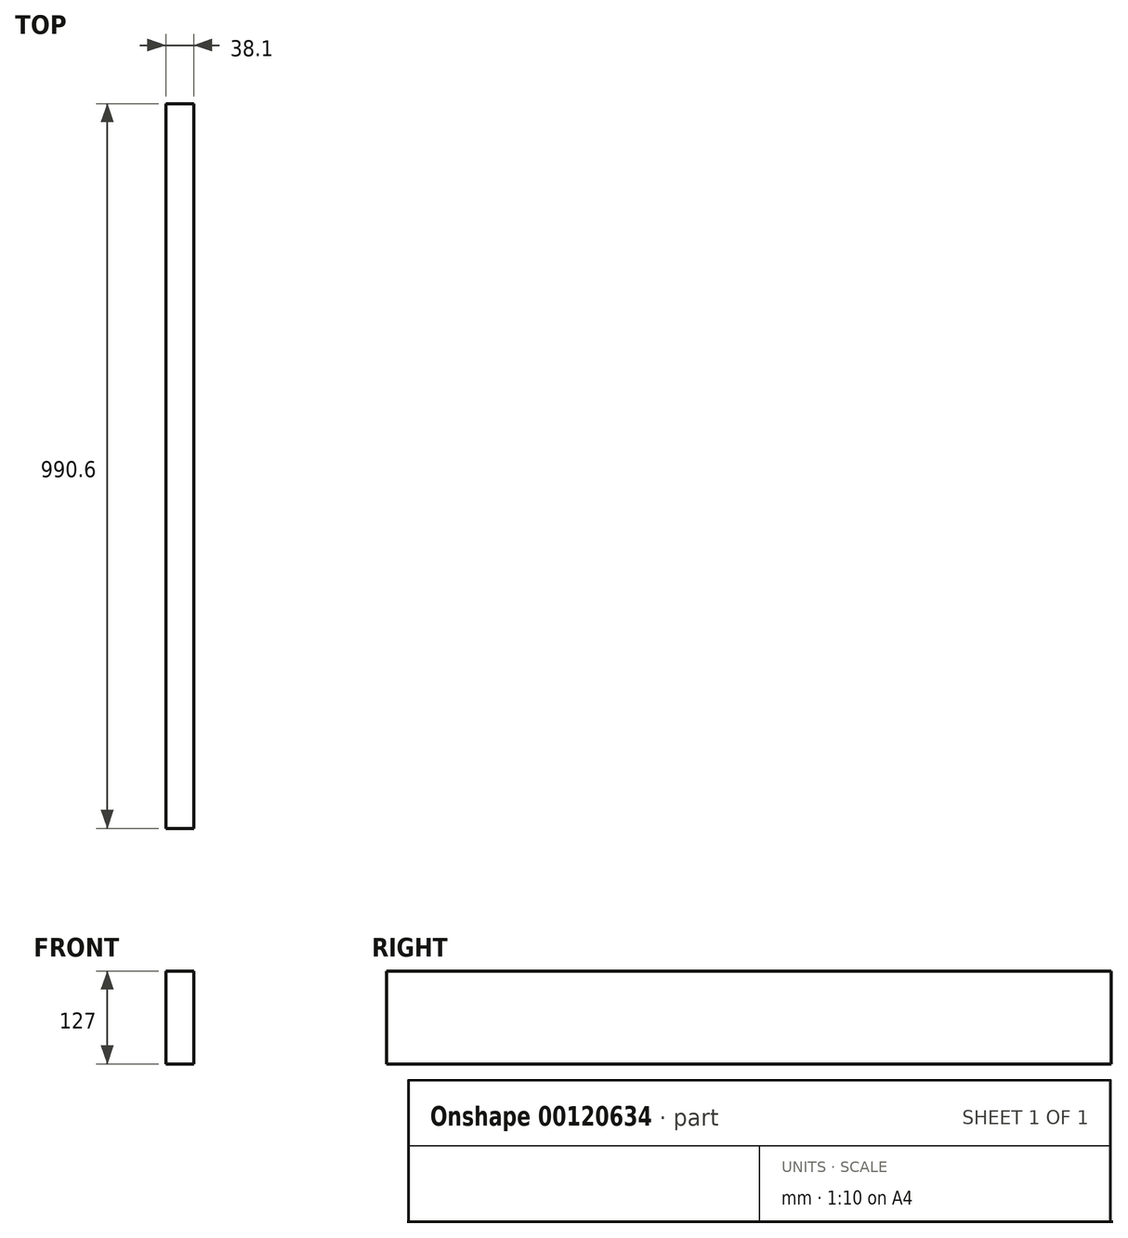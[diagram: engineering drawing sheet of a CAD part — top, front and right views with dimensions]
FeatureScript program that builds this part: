
annotation { "Feature Type Name" : "Feature", "Feature Type Description" : "" }
export const myFeature = defineFeature(function(context is Context, id is Id, definition is map)
    precondition{}
    {
        {
            var Q0;
            Q0=qCreatedBy(makeId("Top.planeOp"),FACE);
            var sketch = newSketch(context, id + "F0", { "sketchPlane" : qUnion([Q0])});
            skLineSegment(sketch, "E0.bottom", {"start": v(-19.05, -495.3) * mm, "end": v(19.05, -495.3) * mm});
            skLineSegment(sketch, "E0.top", {"start": v(-19.05, 495.3) * mm, "end": v(19.05, 495.3) * mm});
            skLineSegment(sketch, "E0.left", {"start": v(-19.05, -495.3) * mm, "end": v(-19.05, 495.3) * mm});
            skLineSegment(sketch, "E0.right", {"start": v(19.05, -495.3) * mm, "end": v(19.05, 495.3) * mm});
            skPoint(sketch, "E0.middle", {"position": v(0, 0) * mm});
            skSolve(sketch);
        }
        {
            var Q0;
            Q0=qSketchRegion(id+"F0",true);
            extrude(context, id + "F1", {"entities" : qUnion([Q0]), "depth" : 127 * mm});
        }
    });
